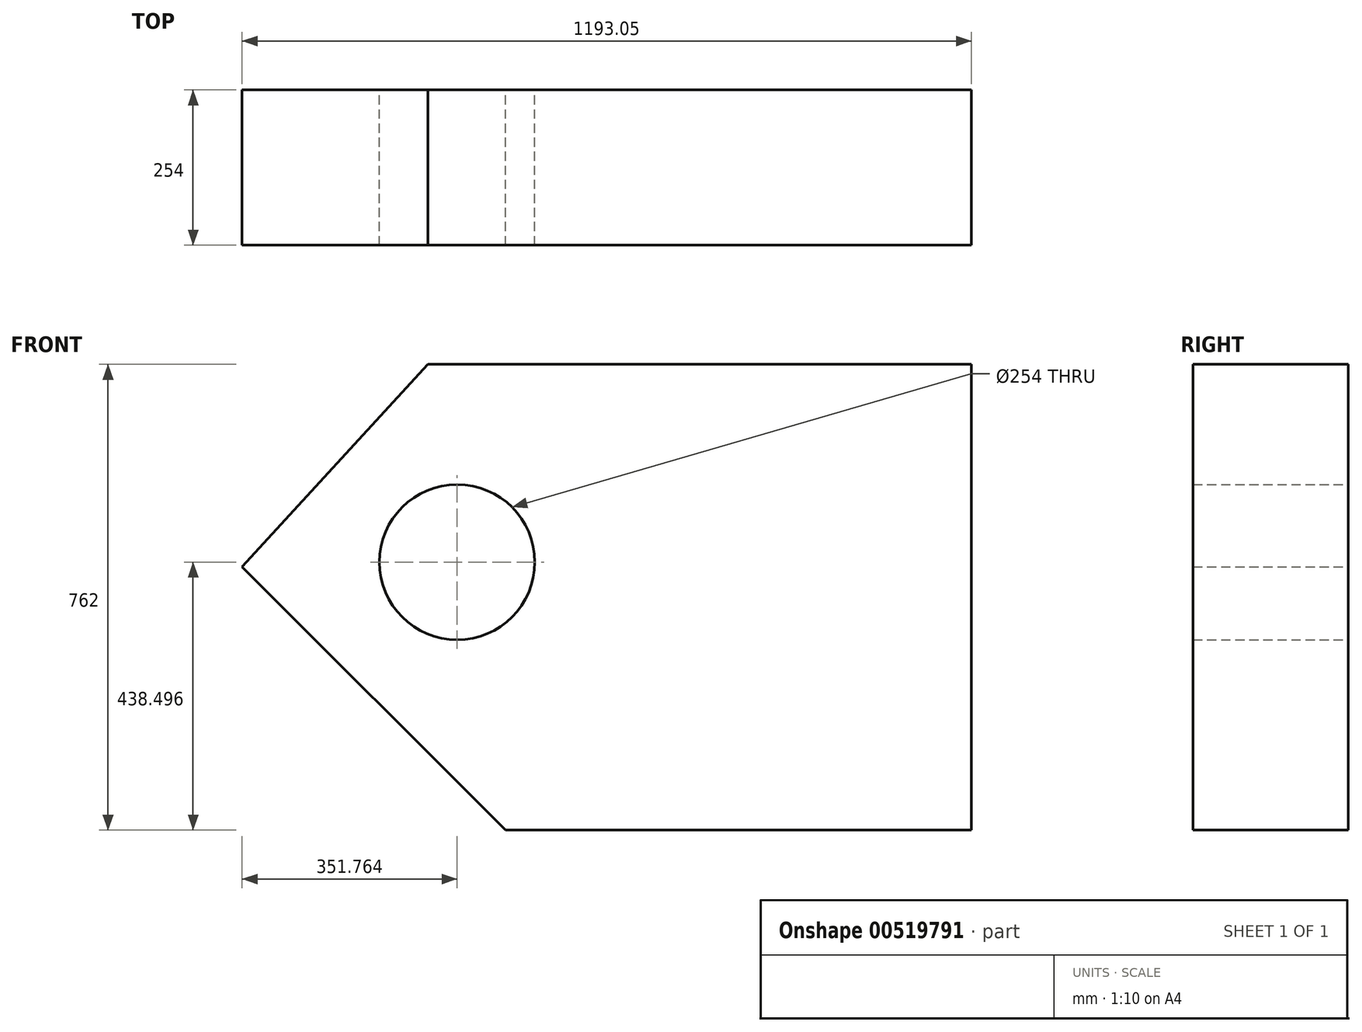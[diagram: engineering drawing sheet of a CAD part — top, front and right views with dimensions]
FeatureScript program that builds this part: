
annotation { "Feature Type Name" : "Feature", "Feature Type Description" : "" }
export const myFeature = defineFeature(function(context is Context, id is Id, definition is map)
    precondition{}
    {
        {
            var Q0;
            Q0=qCreatedBy(makeId("Front.planeOp"),FACE);
            var sketch = newSketch(context, id + "F0", { "sketchPlane" : qUnion([Q0])});
            skLineSegment(sketch, "E0", {"start": v(1193.05, -431.05) * mm, "end": v(431.05, -431.05) * mm});
            skLineSegment(sketch, "E1", {"start": v(304.05, 330.95) * mm, "end": v(0, 0) * mm});
            skLineSegment(sketch, "E2", {"start": v(0, 0) * mm, "end": v(431.05, -431.05) * mm});
            skCircle(sketch, "E3", {"center": v(351.76, 7.45) * mm, "radius": 127 * mm});
            skLineSegment(sketch, "E4", {"start": v(304.05, 330.95) * mm, "end": v(1193.05, 330.95) * mm});
            skLineSegment(sketch, "E5", {"start": v(1193.05, -431.05) * mm, "end": v(1193.05, 330.95) * mm});
            skSolve(sketch);
        }
        {
            var Q0;
            Q0 = qSketchRegion(id + "F0", true);
            extrude(context, id + "F1", {"entities" : qUnion([Q0]), "depth" : 254 * mm, "offsetDistance" : 25.4 * mm});
        }
    });
